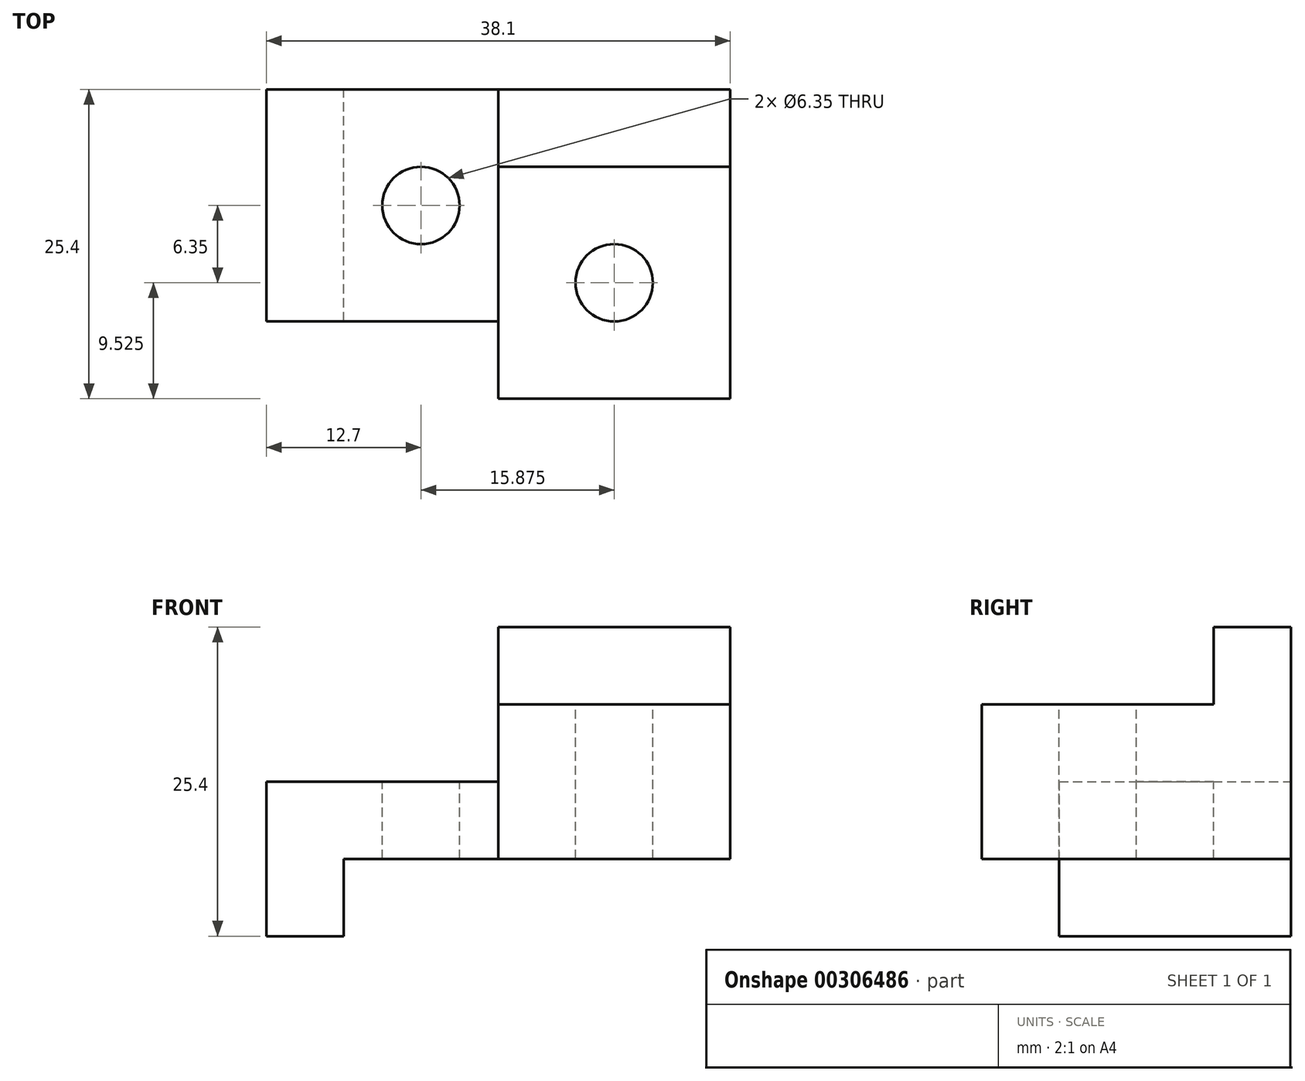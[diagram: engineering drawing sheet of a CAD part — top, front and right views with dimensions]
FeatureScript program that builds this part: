
annotation { "Feature Type Name" : "Feature", "Feature Type Description" : "" }
export const myFeature = defineFeature(function(context is Context, id is Id, definition is map)
    precondition{}
    {
        {
            var Q0;
            Q0=qCreatedBy(makeId("Front.planeOp"),FACE);
            var sketch = newSketch(context, id + "F0", { "sketchPlane" : qUnion([Q0])});
            skLineSegment(sketch, "E0.bottom", {"start": v(0, 6.35) * mm, "end": v(-19.05, 6.35) * mm});
            skLineSegment(sketch, "E0.top", {"start": v(0, 0) * mm, "end": v(-12.7, 0) * mm});
            skLineSegment(sketch, "E0.left", {"start": v(0, 6.35) * mm, "end": v(0, 0) * mm});
            skLineSegment(sketch, "E0.right", {"start": v(-19.05, 6.35) * mm, "end": v(-19.05, 0) * mm});
            skLineSegment(sketch, "E1.top", {"start": v(-19.05, -6.35) * mm, "end": v(-12.7, -6.35) * mm});
            skLineSegment(sketch, "E1.left", {"start": v(-19.05, 0) * mm, "end": v(-19.05, -6.35) * mm});
            skLineSegment(sketch, "E1.right", {"start": v(-12.7, 0) * mm, "end": v(-12.7, -6.35) * mm});
            skSolve(sketch);
        }
        {
            var Q0;
            Q0 = qSketchRegion(id + "F0", true);
            extrude(context, id + "F1", {"entities" : qUnion([Q0]), "depth" : 19.05 * mm});
        }
        {
            var Q0;
            Q0=qCreatedBy(makeId("Right.planeOp"),FACE);
            var sketch = newSketch(context, id + "F2", { "sketchPlane" : qUnion([Q0])});
            skLineSegment(sketch, "E2.bottom", {"start": v(0, 0) * mm, "end": v(-25.4, 0) * mm});
            skLineSegment(sketch, "E2.top", {"start": v(-6.35, 12.7) * mm, "end": v(-25.4, 12.7) * mm});
            skLineSegment(sketch, "E2.left", {"start": v(0, 0) * mm, "end": v(0, 12.7) * mm});
            skLineSegment(sketch, "E2.right", {"start": v(-25.4, 0) * mm, "end": v(-25.4, 12.7) * mm});
            skLineSegment(sketch, "E3.top", {"start": v(-6.35, 19.05) * mm, "end": v(0, 19.05) * mm});
            skLineSegment(sketch, "E3.left", {"start": v(-6.35, 12.7) * mm, "end": v(-6.35, 19.05) * mm});
            skLineSegment(sketch, "E3.right", {"start": v(0, 12.7) * mm, "end": v(0, 19.05) * mm});
            skSolve(sketch);
        }
        {
            var Q0;
            Q0 = qSketchRegion(id + "F2", true);
            extrude(context, id + "F3", {"entities" : qUnion([Q0]), "operationType" : NewBodyOperationType.ADD, "depth" : 19.05 * mm});
        }
        {
            var Q0;
            Q0=makeQuery(id+"F3.opExtrude","SWEPT_FACE",FACE,{"disambiguationData":[OSD([sQuery(id+"F2.wireOp",EDGE,"E2.top")])]});
            var sketch = newSketch(context, id + "F4", { "sketchPlane" : qUnion([Q0])});
            skCircle(sketch, "E4", {"center": v(9.53, -15.88) * mm, "radius": 3.18 * mm});
            skCircle(sketch, "E5", {"center": v(-6.35, -9.53) * mm, "radius": 3.18 * mm});
            skSolve(sketch);
        }
        {
            var Q0;
            Q0 = qSketchRegion(id + "F4", true);
            extrude(context, id + "F5", {"entities" : qUnion([Q0]), "operationType" : NewBodyOperationType.REMOVE, "endBound" : BoundingType.THROUGH_ALL, "oppositeDirection" : true, "depth" : 25.4 * mm});
        }
    });
